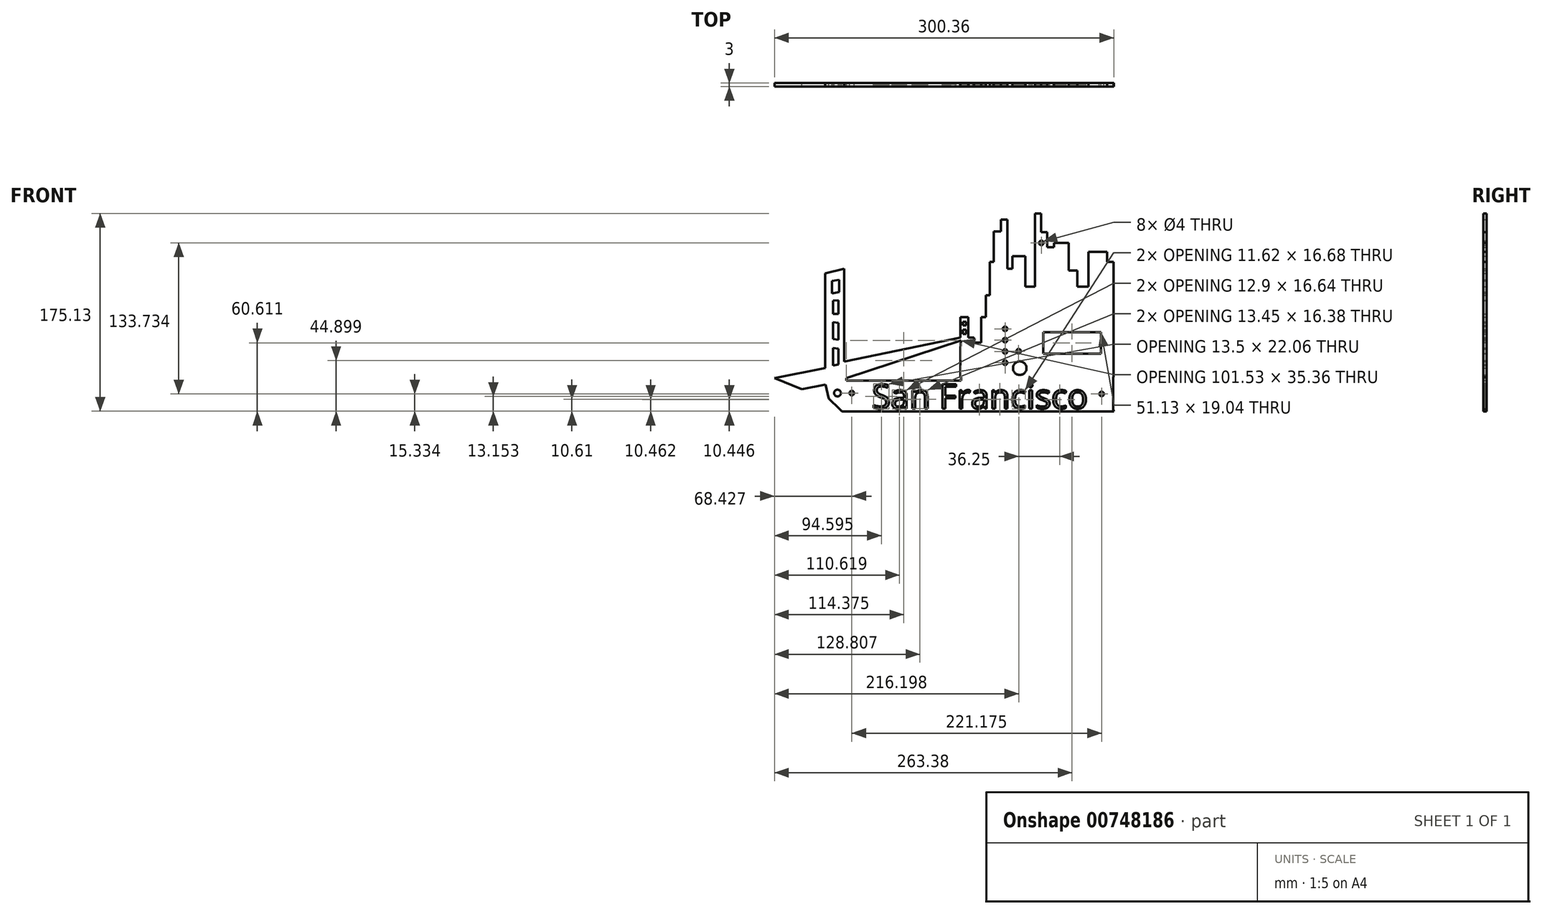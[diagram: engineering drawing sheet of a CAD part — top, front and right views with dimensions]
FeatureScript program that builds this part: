
annotation { "Feature Type Name" : "Feature", "Feature Type Description" : "" }
export const myFeature = defineFeature(function(context is Context, id is Id, definition is map)
    precondition{}
    {
        {
            var Q0;
            Q0=qCreatedBy(makeId("Front.planeOp"),FACE);
            var sketch = newSketch(context, id + "F0", { "sketchPlane" : qUnion([Q0])});
            skLineSegment(sketch, "E0.bottom", {"start": v(2.44, 0) * mm, "end": v(302.44, 0) * mm, "construction": true});
            skLineSegment(sketch, "E0.left", {"start": v(2.44, 0) * mm, "end": v(2.44, -200) * mm, "construction": true});
            skLineSegment(sketch, "E0.right", {"start": v(302.44, 0) * mm, "end": v(302.44, -200) * mm, "construction": true});
            skLineSegment(sketch, "E1", {"start": v(2.44, -150.68) * mm, "end": v(47.3, -141.5) * mm});
            skLineSegment(sketch, "E2", {"start": v(47.3, -141.5) * mm, "end": v(47.3, -57.66) * mm});
            skLineSegment(sketch, "E3", {"start": v(47.3, -57.66) * mm, "end": v(64.28, -53.67) * mm});
            skLineSegment(sketch, "E4", {"start": v(64.28, -53.67) * mm, "end": v(64.28, -136.02) * mm});
            skLineSegment(sketch, "E5", {"start": v(64.28, -136.02) * mm, "end": v(167.09, -114.56) * mm});
            skLineSegment(sketch, "E6", {"start": v(167.09, -114.56) * mm, "end": v(167.09, -96.59) * mm});
            skLineSegment(sketch, "E7", {"start": v(167.09, -96.59) * mm, "end": v(174.08, -96.59) * mm});
            skLineSegment(sketch, "E8", {"start": v(174.08, -96.59) * mm, "end": v(174.08, -114.56) * mm});
            skLineSegment(sketch, "E9", {"start": v(174.08, -114.56) * mm, "end": v(179.07, -114.56) * mm});
            skLineSegment(sketch, "E10", {"start": v(179.07, -114.56) * mm, "end": v(179.07, -119.05) * mm});
            skLineSegment(sketch, "E11", {"start": v(179.07, -119.05) * mm, "end": v(185.56, -119.05) * mm});
            skLineSegment(sketch, "E12", {"start": v(185.56, -119.05) * mm, "end": v(185.56, -96.59) * mm});
            skLineSegment(sketch, "E13", {"start": v(185.56, -96.59) * mm, "end": v(189.55, -96.59) * mm});
            skLineSegment(sketch, "E14", {"start": v(189.55, -96.59) * mm, "end": v(189.55, -77.12) * mm});
            skLineSegment(sketch, "E15", {"start": v(189.55, -77.12) * mm, "end": v(193.04, -77.12) * mm});
            skLineSegment(sketch, "E16", {"start": v(193.04, -77.12) * mm, "end": v(193.04, -47.68) * mm});
            skLineSegment(sketch, "E17", {"start": v(193.04, -47.68) * mm, "end": v(196.54, -47.68) * mm});
            skLineSegment(sketch, "E18", {"start": v(196.54, -47.68) * mm, "end": v(196.54, -20.73) * mm});
            skLineSegment(sketch, "E19", {"start": v(196.54, -20.73) * mm, "end": v(203.02, -20.73) * mm});
            skLineSegment(sketch, "E20", {"start": v(203.02, -20.73) * mm, "end": v(203.02, -10.25) * mm});
            skLineSegment(sketch, "E21", {"start": v(203.02, -10.25) * mm, "end": v(208.51, -10.25) * mm});
            skLineSegment(sketch, "E22", {"start": v(208.51, -10.25) * mm, "end": v(208.51, -53.67) * mm});
            skLineSegment(sketch, "E23", {"start": v(208.51, -53.67) * mm, "end": v(213, -53.67) * mm});
            skLineSegment(sketch, "E24", {"start": v(213, -53.67) * mm, "end": v(213, -42.69) * mm});
            skLineSegment(sketch, "E25", {"start": v(213, -42.69) * mm, "end": v(224.49, -42.69) * mm});
            skLineSegment(sketch, "E26", {"start": v(224.49, -42.69) * mm, "end": v(224.49, -69.64) * mm});
            skLineSegment(sketch, "E27", {"start": v(224.49, -69.64) * mm, "end": v(232.97, -69.64) * mm});
            skLineSegment(sketch, "E28", {"start": v(232.97, -69.64) * mm, "end": v(232.97, -4.76) * mm});
            skLineSegment(sketch, "E29", {"start": v(232.97, -4.76) * mm, "end": v(238.46, -4.76) * mm});
            skLineSegment(sketch, "E30", {"start": v(238.46, -4.76) * mm, "end": v(238.46, -21.23) * mm});
            skLineSegment(sketch, "E31", {"start": v(238.46, -21.23) * mm, "end": v(243.95, -21.23) * mm});
            skLineSegment(sketch, "E32", {"start": v(243.95, -21.23) * mm, "end": v(243.95, -34.7) * mm});
            skLineSegment(sketch, "E33", {"start": v(243.95, -34.7) * mm, "end": v(249.94, -34.7) * mm});
            skLineSegment(sketch, "E34", {"start": v(249.94, -34.7) * mm, "end": v(249.94, -30.7) * mm});
            skLineSegment(sketch, "E35", {"start": v(249.94, -30.7) * mm, "end": v(262.92, -30.7) * mm});
            skLineSegment(sketch, "E36", {"start": v(262.92, -30.7) * mm, "end": v(262.92, -55.16) * mm});
            skLineSegment(sketch, "E37", {"start": v(262.92, -55.16) * mm, "end": v(270.4, -55.16) * mm});
            skLineSegment(sketch, "E38", {"start": v(270.4, -55.16) * mm, "end": v(270.4, -69.64) * mm});
            skLineSegment(sketch, "E39", {"start": v(270.4, -69.64) * mm, "end": v(280.38, -69.64) * mm});
            skLineSegment(sketch, "E40", {"start": v(280.38, -69.64) * mm, "end": v(280.38, -38.7) * mm});
            skLineSegment(sketch, "E41", {"start": v(280.38, -38.7) * mm, "end": v(296.85, -38.7) * mm});
            skLineSegment(sketch, "E42", {"start": v(296.85, -38.7) * mm, "end": v(296.85, -47.68) * mm});
            skLineSegment(sketch, "E43", {"start": v(296.85, -47.68) * mm, "end": v(302.44, -47.68) * mm});
            skLineSegment(sketch, "E44", {"start": v(302.44, -47.68) * mm, "end": v(302.44, -124.04) * mm});
            skLineSegment(sketch, "E45", {"start": v(302.44, -124.04) * mm, "end": v(167.09, -124.04) * mm});
            skLineSegment(sketch, "E46", {"start": v(167.09, -124.04) * mm, "end": v(167.5, -117.3) * mm});
            skLineSegment(sketch, "E47", {"start": v(2.44, -150.68) * mm, "end": v(26.69, -160.4) * mm});
            skLineSegment(sketch, "E48", {"start": v(26.69, -160.4) * mm, "end": v(47.78, -156.1) * mm});
            skLineSegment(sketch, "E49", {"start": v(47.78, -156.1) * mm, "end": v(50.34, -168.64) * mm});
            skLineSegment(sketch, "E50", {"start": v(50.34, -168.64) * mm, "end": v(60.16, -178.16) * mm});
            skLineSegment(sketch, "E51", {"start": v(60.16, -178.16) * mm, "end": v(66.05, -178.16) * mm});
            skLineSegment(sketch, "E52", {"start": v(66.05, -178.16) * mm, "end": v(66.05, -150.68) * mm});
            skLineSegment(sketch, "E53", {"start": v(66.05, -150.68) * mm, "end": v(167.5, -117.3) * mm});
            skLineSegment(sketch, "E54", {"start": v(54.4, -123.98) * mm, "end": v(54.4, -139.36) * mm});
            skLineSegment(sketch, "E55", {"start": v(54.4, -139.36) * mm, "end": v(59.14, -138.5) * mm});
            skLineSegment(sketch, "E56", {"start": v(59.14, -138.5) * mm, "end": v(59.14, -124.64) * mm});
            skLineSegment(sketch, "E57", {"start": v(59.14, -124.64) * mm, "end": v(54.4, -123.98) * mm});
            skLineSegment(sketch, "E58", {"start": v(54.4, -115.9) * mm, "end": v(59.14, -116.57) * mm});
            skLineSegment(sketch, "E59", {"start": v(59.14, -116.57) * mm, "end": v(59.14, -101.57) * mm});
            skLineSegment(sketch, "E60", {"start": v(59.14, -101.57) * mm, "end": v(54.4, -100.91) * mm});
            skLineSegment(sketch, "E61", {"start": v(54.4, -100.91) * mm, "end": v(54.4, -115.9) * mm});
            skLineSegment(sketch, "E62", {"start": v(59.14, -81.48) * mm, "end": v(59.14, -93.63) * mm});
            skLineSegment(sketch, "E63", {"start": v(59.14, -93.63) * mm, "end": v(54.4, -93.63) * mm});
            skLineSegment(sketch, "E64", {"start": v(54.4, -93.63) * mm, "end": v(54.4, -82.02) * mm});
            skLineSegment(sketch, "E65", {"start": v(54.4, -82.02) * mm, "end": v(59.14, -81.48) * mm});
            skLineSegment(sketch, "E66", {"start": v(53.43, -64.37) * mm, "end": v(53.43, -75.53) * mm});
            skLineSegment(sketch, "E67", {"start": v(53.43, -75.53) * mm, "end": v(59.63, -74.23) * mm});
            skLineSegment(sketch, "E68", {"start": v(59.63, -74.23) * mm, "end": v(59.63, -63.62) * mm});
            skLineSegment(sketch, "E69", {"start": v(59.63, -63.62) * mm, "end": v(53.43, -64.37) * mm});
            skPoint(sketch, "E70.startSnap0", {"position": v(59.63, -68.92) * mm});
            skLineSegment(sketch, "E71", {"start": v(169.1, -100.56) * mm, "end": v(169.1, -103.8) * mm});
            skLineSegment(sketch, "E72", {"start": v(169.1, -103.8) * mm, "end": v(172.08, -103.8) * mm});
            skLineSegment(sketch, "E73", {"start": v(172.08, -103.8) * mm, "end": v(172.08, -100.56) * mm});
            skLineSegment(sketch, "E74", {"start": v(172.08, -100.56) * mm, "end": v(169.1, -100.56) * mm});
            skLineSegment(sketch, "E75", {"start": v(172.08, -107.77) * mm, "end": v(169.1, -107.77) * mm});
            skLineSegment(sketch, "E76", {"start": v(169.1, -107.77) * mm, "end": v(169.1, -111.42) * mm});
            skLineSegment(sketch, "E77", {"start": v(169.1, -111.42) * mm, "end": v(172.08, -111.42) * mm});
            skLineSegment(sketch, "E78", {"start": v(172.08, -111.42) * mm, "end": v(172.08, -107.77) * mm});
            skLineSegment(sketch, "E79", {"start": v(167.09, -124.04) * mm, "end": v(167.09, -149.53) * mm});
            skLineSegment(sketch, "E80", {"start": v(167.09, -149.53) * mm, "end": v(302.44, -149.53) * mm});
            skLineSegment(sketch, "E81", {"start": v(302.44, -149.53) * mm, "end": v(302.44, -124.04) * mm});
            skSolve(sketch);
        }
        {
            var Q0;
            Q0 = qSketchRegion(id + "F0", true);
            extrude(context, id + "F1", {"entities" : qUnion([Q0]), "depth" : 3 * mm, "offsetDistance" : 25 * mm});
        }
        {
            var Q0;
            Q0=qCreatedBy(makeId("Front.planeOp"),FACE);
            var sketch = newSketch(context, id + "F2", { "sketchPlane" : qUnion([Q0])});
            skLineSegment(sketch, "E82", {"start": v(302.28, -124.39) * mm, "end": v(302.28, -178.01) * mm});
            skLineSegment(sketch, "E83", {"start": v(302.28, -178.01) * mm, "end": v(65.72, -178.01) * mm});
            skLineSegment(sketch, "E84", {"start": v(296.33, -178.01) * mm, "end": v(296.33, -123.85) * mm});
            skLineSegment(sketch, "E85", {"start": v(60.17, -178.15) * mm, "end": v(62.1, -179.9) * mm});
            skLineSegment(sketch, "E86", {"start": v(62.1, -179.9) * mm, "end": v(302.8, -179.9) * mm});
            skLineSegment(sketch, "E87", {"start": v(302.8, -179.9) * mm, "end": v(302.28, -178.01) * mm});
            skLineSegment(sketch, "E88", {"start": v(60.17, -178.15) * mm, "end": v(65.72, -178.01) * mm});
            skLineSegment(sketch, "E89", {"start": v(296.33, -152.67) * mm, "end": v(72.22, -152.67) * mm});
            skLineSegment(sketch, "E90", {"start": v(72.22, -152.67) * mm, "end": v(72.22, -178.01) * mm});
            skLineSegment(sketch, "E91", {"start": v(167.58, -124.47) * mm, "end": v(167.58, -152.67) * mm});
            skLineSegment(sketch, "E92", {"start": v(167.58, -152.67) * mm, "end": v(167.58, -124.47) * mm});
            skLineSegment(sketch, "E93", {"start": v(173.95, -124.47) * mm, "end": v(173.95, -152.67) * mm});
            skLineSegment(sketch, "E94", {"start": v(173.95, -152.67) * mm, "end": v(167.58, -152.67) * mm});
            skLineSegment(sketch, "E95", {"start": v(167.58, -124.47) * mm, "end": v(167.58, -124.1) * mm});
            skLineSegment(sketch, "E96", {"start": v(167.58, -124.1) * mm, "end": v(167.58, -124.03) * mm});
            skLineSegment(sketch, "E97", {"start": v(167.58, -124.03) * mm, "end": v(173.95, -124.03) * mm});
            skLineSegment(sketch, "E98", {"start": v(173.95, -124.03) * mm, "end": v(173.95, -124.47) * mm});
            skLineSegment(sketch, "E99", {"start": v(296.33, -123.85) * mm, "end": v(302.25, -123.85) * mm});
            skLineSegment(sketch, "E100", {"start": v(302.25, -123.85) * mm, "end": v(302.28, -124.39) * mm});
            skLineSegment(sketch, "E101", {"start": v(72.22, -152.67) * mm, "end": v(66.12, -152.67) * mm});
            skLineSegment(sketch, "E102", {"start": v(66.12, -152.67) * mm, "end": v(65.72, -178.01) * mm});
            skLineSegment(sketch, "E103", {"start": v(66.12, -152.67) * mm, "end": v(65.86, -152.67) * mm});
            skLineSegment(sketch, "E104", {"start": v(65.86, -152.67) * mm, "end": v(65.97, -162.25) * mm});
            skLineSegment(sketch, "E105", {"start": v(173.95, -149.21) * mm, "end": v(173.95, -152.67) * mm});
            skLineSegment(sketch, "E106", {"start": v(296.33, -152.67) * mm, "end": v(296.33, -150.93) * mm});
            skLineSegment(sketch, "E107", {"start": v(296.33, -150.93) * mm, "end": v(173.95, -149.21) * mm});
            skLineSegment(sketch, "E108", {"start": v(296.03, -149.14) * mm, "end": v(173.95, -149.21) * mm});
            skLineSegment(sketch, "E109", {"start": v(296.03, -149.14) * mm, "end": v(296.33, -149.14) * mm});
            skLineSegment(sketch, "E110", {"start": v(296.33, -149.14) * mm, "end": v(296.3, -150.9) * mm});
            skSolve(sketch);
        }
        {
            var Q0;
            Q0=qCreatedBy(makeId("Front.planeOp"),FACE);
            var sketch = newSketch(context, id + "F3", { "sketchPlane" : qUnion([Q0])});
            skLineSegment(sketch, "E111.bottom", {"start": v(240.26, -109.76) * mm, "end": v(291.39, -109.76) * mm});
            skLineSegment(sketch, "E111.top", {"start": v(240.26, -128.8) * mm, "end": v(291.39, -128.8) * mm});
            skLineSegment(sketch, "E111.left", {"start": v(240.26, -109.76) * mm, "end": v(240.26, -128.8) * mm});
            skLineSegment(sketch, "E111.right", {"start": v(291.39, -109.76) * mm, "end": v(291.39, -128.8) * mm});
            skCircle(sketch, "E112", {"center": v(206.56, -116.91) * mm, "radius": 2 * mm});
            skCircle(sketch, "E113", {"center": v(206.56, -126.91) * mm, "radius": 2 * mm});
            skCircle(sketch, "E114", {"center": v(218.56, -126.72) * mm, "radius": 2 * mm});
            skCircle(sketch, "E115", {"center": v(206.56, -136.91) * mm, "radius": 2 * mm});
            skCircle(sketch, "E116", {"center": v(206.56, -106.91) * mm, "radius": 2 * mm});
            skCircle(sketch, "E117", {"center": v(219.56, -141.72) * mm, "radius": 6 * mm});
            skCircle(sketch, "E118", {"center": v(58.23, -163.8) * mm, "radius": 3 * mm});
            skSolve(sketch);
        }
        {
            var Q0;
            Q0 = qSketchRegion(id + "F3", true);
            extrude(context, id + "F4", {"entities" : qUnion([Q0]), "operationType" : NewBodyOperationType.REMOVE, "depth" : 53 * mm, "offsetDistance" : 25 * mm});
        }
        {
            var Q0;
            Q0 = qSketchRegion(id + "F2", true);
            extrude(context, id + "F5", {"entities" : qUnion([Q0]), "operationType" : NewBodyOperationType.ADD, "depth" : 3 * mm, "offsetDistance" : 25 * mm});
        }
        {
            var Q0;
            Q0=qCreatedBy(makeId("Front.planeOp"),FACE);
            var sketch = newSketch(context, id + "F6", { "sketchPlane" : qUnion([Q0])});
            skText(sketch, "E119", { "text": "San Francisco ", "fontName": "OpenSans-Regular.ttf"});
            skLineSegment(sketch, "E120", {"start": v(167.5, -117.32) * mm, "end": v(167.5, -124.03) * mm});
            const initialGuessF6  = {"E119": [0.08873, -0.17747, 1, 0, 0.02164]};
            skSetInitialGuess(sketch, initialGuessF6);
            skSolve(sketch);
        }
        {
            var Q0;
            Q0 = qSketchRegion(id + "F6", true);
            extrude(context, id + "F7", {"entities" : qUnion([Q0]), "operationType" : NewBodyOperationType.REMOVE, "depth" : 8.3 * mm, "offsetDistance" : 25 * mm});
        }
        {
            var Q0;
            Q0 = qSketchRegion(id + "F6", true);
            extrude(context, id + "F8", {"entities" : qUnion([Q0]), "depth" : 1.2 * mm, "offsetDistance" : 25 * mm});
        }
        {
            var Q0;
            Q0=qCreatedBy(makeId("Front.planeOp"),FACE);
            var sketch = newSketch(context, id + "F9", { "sketchPlane" : qUnion([Q0])});
            skCircle(sketch, "E121", {"center": v(238.63, -30.82) * mm, "radius": 2 * mm});
            skCircle(sketch, "E122", {"center": v(292.04, -164.56) * mm, "radius": 2 * mm});
            skCircle(sketch, "E123", {"center": v(70.87, -163.76) * mm, "radius": 2 * mm});
            skSolve(sketch);
        }
        {
            var Q0;
            Q0 = qSketchRegion(id + "F9", true);
            extrude(context, id + "F10", {"entities" : qUnion([Q0]), "operationType" : NewBodyOperationType.REMOVE, "depth" : 36 * mm, "offsetDistance" : 25 * mm});
        }
        {
            var Q0;
            Q0 = qSketchRegion(id + "F3", true);
            extrude(context, id + "F11", {"entities" : qUnion([Q0]), "operationType" : NewBodyOperationType.REMOVE, "oppositeDirection" : true, "depth" : 80 * mm, "offsetDistance" : 25 * mm});
        }
    });
